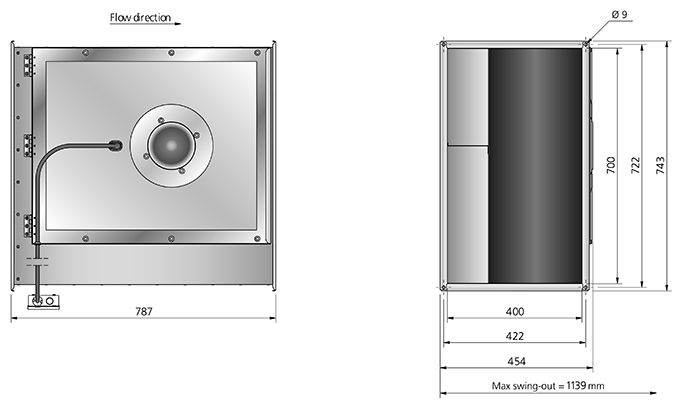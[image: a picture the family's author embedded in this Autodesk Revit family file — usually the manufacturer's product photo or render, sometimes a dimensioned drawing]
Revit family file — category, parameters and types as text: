
# Revit family: RKB 700X400 E3 ErP AC_7480164
name_source: partatom
category: Mechanical Equipment
revit_build: Autodesk Revit MEP 2014 (Build: 20130308_1515(x64)
units: mm (PartAtom-declared; Revit-internal decimal feet)

## types (1)
- RKB 700X400 E3 ErP AC
    Capacitor = - μF
    Connector Height = 400 mm  [stored 1.31234 ft]
    Connector Width = 700 mm  [stored 2.29659 ft]
    Current = 2 A
    Depth = 743 mm  [stored 2.43766 ft]
    Description = UNINSULATED DUCT FANS WITH RECTANGULAR CONNECTIONS
    Frequency = 50 Hz
    Height = 454 mm  [stored 1.4895 ft]
    Main Material = Steel, Galvanized
    Max. temperature of transported air = 40 °C
    Max. temperature of transported air when speed controlled = 40 °C
    Phase = 3
    Power = 830 W
    Sound pressure level at 3 m = 60 dB(A)
    Speed = 1430 rpm
    Voltage = 400 V
    Voltage range = 380-418 V
    Weight = 48.40 kg
    Width = 787 mm  [stored 2.58202 ft]
    Wiring diagram = Y 4040004 / Δ4040003

note: [stored X ft] marks values corroborated as IEEE doubles in the binary element streams (Revit-internal decimal feet)

## geometry (parser evidence)
native form markers: Sweep x4
no freeform markers — native parametric forms only
